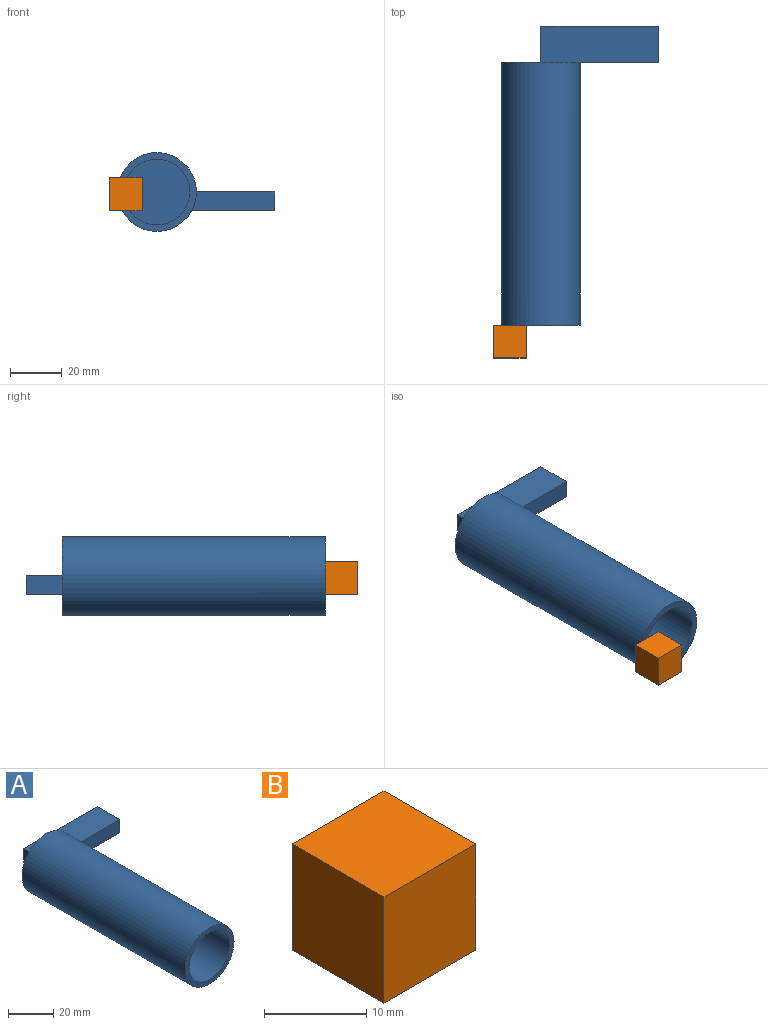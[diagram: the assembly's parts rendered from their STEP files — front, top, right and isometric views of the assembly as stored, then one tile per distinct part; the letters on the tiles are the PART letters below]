
ASSEMBLY  parts=2 mates=1
PART A: 11 faces, bbox 60.8x115.6x30.5 mm
  f0: cylinder r=15.24mm len=101.6mm, axis (0,1,0), area 9728.8mm2, adj f1,f2,f9
  f1: plane 30.48x30.48mm, normal (0,-1,0), area 223mm2, adj f0,f3
  f2: plane 30.48x30.48mm, normal (0,1,0), area 624.7mm2, adj f0,f5,f6,f7
  f3: cylinder r=12.7mm len=99.06mm, axis (0,1,0), area 7904.6mm2, adj f1,f4
  f4: plane 25.4x25.4mm, normal (0,-1,0), area 506.7mm2, adj f3
  f5: plane 45.53x14mm, normal (0,0,-1), area 637.3mm2, adj f2,f6,f8,f9,f10
  f6: plane 14x7.16mm, normal (-1,0,0), area 100.2mm2, adj f2,f5,f7,f10
  f7: plane 45.53x14mm, normal (0,0,1), area 637.3mm2, adj f2,f6,f8,f9,f10
  f8: plane 14x7.16mm, normal (1,0,0), area 100.2mm2, adj f5,f7,f9,f10
  f9: plane 32.08x7.16mm, normal (0,-1,0), area 221.1mm2, adj f0,f5,f7,f8
  f10: plane 45.53x7.16mm, normal (0,1,0), area 326.1mm2, adj f5,f6,f7,f8
PART B: 6 faces, bbox 12.7x12.7x12.7 mm
  f0: plane 12.7x12.7mm, normal (0,0,-1), area 161.3mm2, adj f1,f3,f4,f5
  f1: plane 12.7x12.7mm, normal (1,0,0), area 161.3mm2, adj f0,f2,f4,f5
  f2: plane 12.7x12.7mm, normal (0,0,1), area 161.3mm2, adj f1,f3,f4,f5
  f3: plane 12.7x12.7mm, normal (-1,0,0), area 161.3mm2, adj f0,f2,f4,f5
  f4: plane 12.7x12.7mm, normal (0,-1,0), area 161.3mm2, adj f0,f1,f2,f3
  f5: plane 12.7x12.7mm, normal (0,1,0), area 161.3mm2, adj f0,f1,f2,f3
PLACE A t=(-82.65,90.72,21.49)mm
PLACE B t=(-94.68,-10.88,-7.99)mm
MATE planar B.f5 <-> A.f0  axis (0,1,0) through (-94.68,-10.88,20.58)mm
